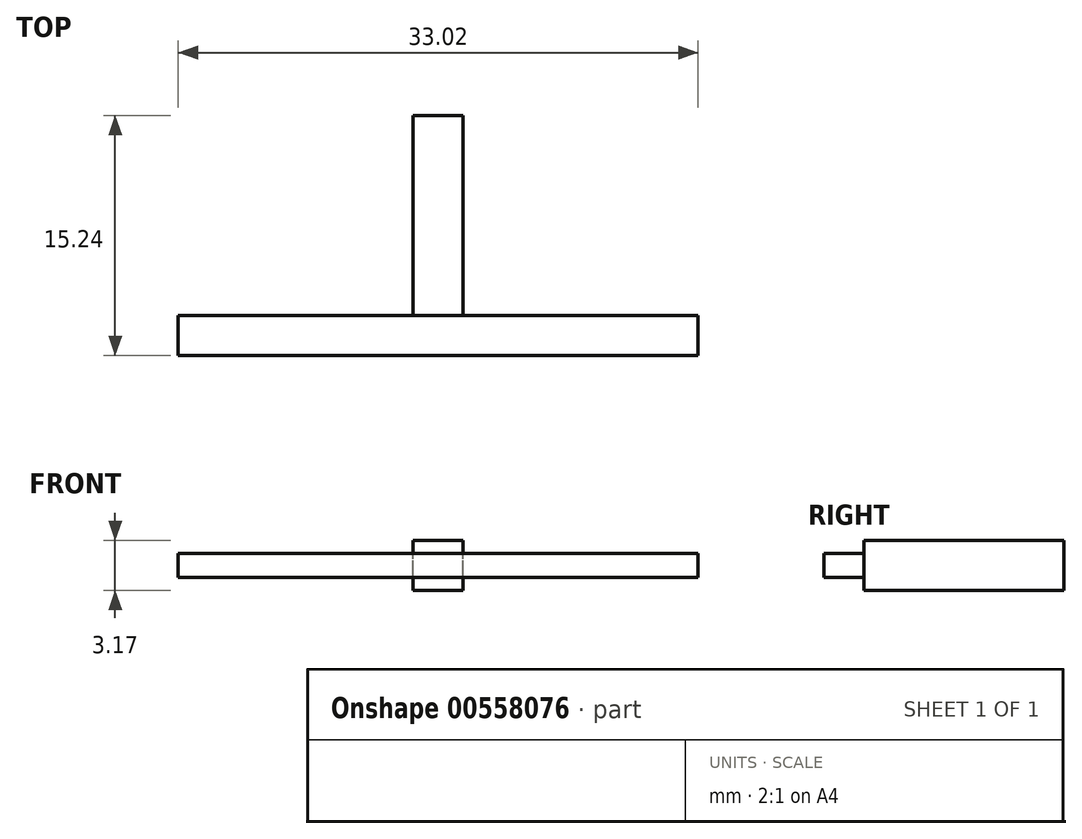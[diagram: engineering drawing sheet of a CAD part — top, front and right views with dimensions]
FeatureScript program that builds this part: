
annotation { "Feature Type Name" : "Feature", "Feature Type Description" : "" }
export const myFeature = defineFeature(function(context is Context, id is Id, definition is map)
    precondition{}
    {
        {
            var Q0;
            Q0=qCreatedBy(makeId("Front.planeOp"),FACE);
            var sketch = newSketch(context, id + "F0", { "sketchPlane" : qUnion([Q0])});
            skLineSegment(sketch, "E0.bottom", {"start": v(-33.76, 9.27) * mm, "end": v(-36.94, 9.27) * mm});
            skLineSegment(sketch, "E0.top", {"start": v(-33.76, 12.44) * mm, "end": v(-36.94, 12.44) * mm});
            skLineSegment(sketch, "E0.left", {"start": v(-33.76, 9.27) * mm, "end": v(-33.76, 12.44) * mm});
            skLineSegment(sketch, "E0.right", {"start": v(-36.94, 9.27) * mm, "end": v(-36.94, 12.44) * mm});
            skPoint(sketch, "E0.middle", {"position": v(-35.35, 10.86) * mm});
            skSolve(sketch);
        }
        {
            var Q0;
            Q0=makeQuery(id+"F0.imprint","IMPRINT",FACE,{"disambiguationData":[TD([[makeQuery(id+"F0.imprint","IMPRINT",EDGE,{"derivedFrom":sQuery(id+"F0.wireOp",EDGE,"E0.bottom")}),-1.0]])]});
            extrude(context, id + "F1", {"entities" : qUnion([Q0]), "depth" : 12.7 * mm, "offsetDistance" : 25.4 * mm});
        }
        {
            var Q0;
            Q0=makeQuery(id+"F1.opExtrude","CAP_FACE",FACE,{"disambiguationData":[OSD([sQuery(id+"F0.wireOp",EDGE,"E0.bottom"),sQuery(id+"F0.wireOp",EDGE,"E0.top"),sQuery(id+"F0.wireOp",EDGE,"E0.left"),sQuery(id+"F0.wireOp",EDGE,"E0.right")])],"isStart":false});
            var sketch = newSketch(context, id + "F2", { "sketchPlane" : qUnion([Q0])});
            skLineSegment(sketch, "E1", {"start": v(-35.35, 12.44) * mm, "end": v(-35.35, 9.27) * mm});
            skLineSegment(sketch, "E2", {"start": v(-36.94, 10.86) * mm, "end": v(-33.76, 10.86) * mm});
            skLineSegment(sketch, "E3.bottom", {"start": v(-51.86, 10.1) * mm, "end": v(-18.84, 10.1) * mm});
            skLineSegment(sketch, "E3.top", {"start": v(-51.86, 11.6) * mm, "end": v(-18.84, 11.6) * mm});
            skLineSegment(sketch, "E3.left", {"start": v(-51.86, 10.1) * mm, "end": v(-51.86, 11.6) * mm});
            skLineSegment(sketch, "E3.right", {"start": v(-18.84, 10.1) * mm, "end": v(-18.84, 11.6) * mm});
            skPoint(sketch, "E3.middle", {"position": v(-35.35, 10.86) * mm});
            skSolve(sketch);
        }
        {
            var Q0;
            Q0 = qSketchRegion(id + "F2", true);
            extrude(context, id + "F3", {"entities" : qUnion([Q0]), "operationType" : NewBodyOperationType.ADD, "depth" : 2.54 * mm, "offsetDistance" : 25.4 * mm});
        }
    });
